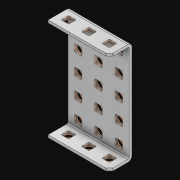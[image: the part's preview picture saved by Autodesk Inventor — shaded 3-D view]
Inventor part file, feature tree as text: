
AUTODESK INVENTOR PART (.ipt)
format: ipt  version: 2021 (Build 250183000, 183)  size: 2,793,984 bytes
history: native  units: in
note: dims shown in document units (in); Inventor stores cm internally (conversion verified against a paired STEP export)
features: extrude x22, other x21, sketch x4, thicken_offset x3, pattern_linear x3, imported_body x1
ambient origin geometry x8: Origin, YZ Plane, XZ Plane, XY Plane, X Axis, Y Axis, Z Axis, Center Point
bodies: Solid1 (feature_tree)
feature tree (54):
  thicken_offset  "Thicken1"
  thicken_offset  "Thicken2"
  thicken_offset  "Thicken3"
  pattern_linear  "Rectangular Pattern1"  Spacing1=0.001in  [1 undecoded]
  pattern_linear  "Rectangular Pattern2"  Spacing1=0.001in  [1 undecoded]
  pattern_linear  "Rectangular Pattern3"  Spacing1=0.182in  [1 undecoded]
  extrude  "Extrusion1"  Depth=0.063in TaperAngle=0.0deg
  sketch  "Sketch1"  dims[d0=0.001in]
  other  "Srf1"
  sketch  "Sketch2"  dims[d1=0.001in]
  other  "Srf2"
  sketch  "Sketch3"  dims[d2=0.001in]
  other  "Srf3"
  other  "Srf4"
  other  "Srf5"
  other  "Srf38"
  other  "Srf39"
  other  "Srf72"
  other  "Srf73"
  other  "Srf106"
  other  "Srf107"
  other  "Srf108"
  other  "Srf141"
  other  "Srf142"
  other  "Srf143"
  other  "Srf176"
  other  "Srf177"
  other  "Srf178"
  other  "Srf211"
  other  "Srf212"
  other  "Srf213"
  sketch  "Sketch4"  dims[d3=0.001in d4=0.001in d5=0.001in d6=0.182in d7=0.063in d8=0.0in d9=0.182in d10=0.063in d11=0.0in d12=0.182in d13=0.063in d14=0.0in d17=0.5in d18=1.1811in d20=0.5in d21=1.1811in d23=0.5in d24=1.9685in d26=0.5in d27=16.0in d28=0.0in]
  imported_body  "Imported1"
  extrude  "ExtrusionSrf1"  Depth=0.182in
  extrude  "ExtrusionSrf2"  Depth=0.063in TaperAngle=0.0deg
  extrude  "ExtrusionSrf3"  Depth=0.182in
  extrude  "ExtrusionSrf4"  Depth=0.063in TaperAngle=0.0deg
  extrude  "ExtrusionSrf5"  Depth=0.5in
  extrude  "ExtrusionSrf38"  Depth=0.5in
  extrude  "ExtrusionSrf39"  Depth=0.5in
  extrude  "ExtrusionSrf72"  Depth=0.5in
  extrude  "ExtrusionSrf73"  Depth=0.5in
  extrude  "ExtrusionSrf106"  Depth=0.5in
  extrude  "ExtrusionSrf107"  Depth=0.5in
  extrude  "ExtrusionSrf108"  TaperAngle=0.0deg  [1 undecoded]
  extrude  "ExtrusionSrf141"  [1 undecoded]
  extrude  "ExtrusionSrf142"  [1 undecoded]
  extrude  "ExtrusionSrf143"  [1 undecoded]
  extrude  "ExtrusionSrf176"  [1 undecoded]
  extrude  "ExtrusionSrf177"  [1 undecoded]
  extrude  "ExtrusionSrf178"  [1 undecoded]
  extrude  "ExtrusionSrf211"  [1 undecoded]
  extrude  "ExtrusionSrf212"  [1 undecoded]
  extrude  "ExtrusionSrf213"  [1 undecoded]
note: 13 required parameter values undecoded (feature->parameter linkage not recoverable at this tier; creation-order binding heuristic only, values carry confidence <= 0.55)
